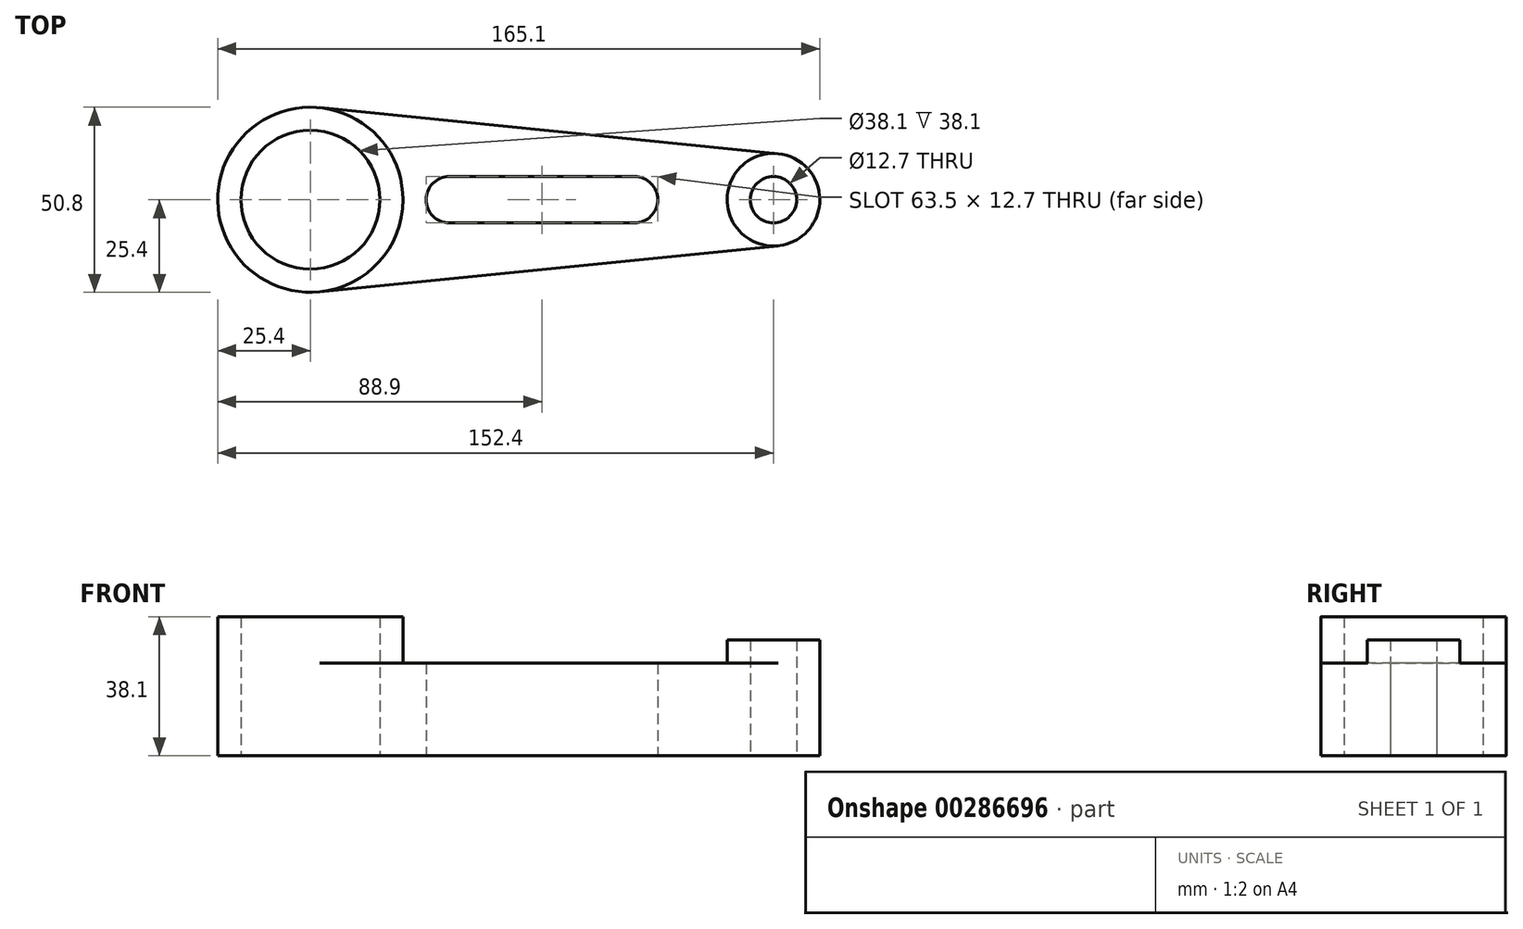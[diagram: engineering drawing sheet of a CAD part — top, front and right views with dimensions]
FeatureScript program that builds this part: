
annotation { "Feature Type Name" : "Feature", "Feature Type Description" : "" }
export const myFeature = defineFeature(function(context is Context, id is Id, definition is map)
    precondition{}
    {
        {
            var Q0;
            Q0=qCreatedBy(makeId("Top.planeOp"),FACE);
            var sketch = newSketch(context, id + "F0", { "sketchPlane" : qUnion([Q0])});
            skArc(sketch, "E0", {"start": v(0, 6.35) * mm, "mid": v(-6.35, 0) * mm, "end": v(0, -6.35) * mm});
            skLineSegment(sketch, "E1", {"start": v(0, -6.35) * mm, "end": v(50.8, -6.35) * mm});
            skLineSegment(sketch, "E2", {"start": v(0, 6.35) * mm, "end": v(50.8, 6.35) * mm});
            skArc(sketch, "E3", {"start": v(50.8, 6.35) * mm, "mid": v(57.15, 0) * mm, "end": v(50.8, -6.35) * mm});
            skCircle(sketch, "E4", {"center": v(88.9, 0) * mm, "radius": 6.35 * mm});
            skCircle(sketch, "E5", {"center": v(88.9, 0) * mm, "radius": 12.7 * mm});
            skCircle(sketch, "E6", {"center": v(-38.1, 0) * mm, "radius": 19.05 * mm});
            skCircle(sketch, "E7", {"center": v(-38.1, 0) * mm, "radius": 25.4 * mm});
            skLineSegment(sketch, "E8", {"start": v(90.17, 12.64) * mm, "end": v(-35.56, 25.27) * mm});
            skLineSegment(sketch, "E9", {"start": v(-35.56, -25.27) * mm, "end": v(90.17, -12.64) * mm});
            skSolve(sketch);
        }
        {
            var Q0;
            Q0=makeQuery(id+"F0.imprint","IMPRINT",FACE,{"disambiguationData":[TD([[makeQuery(id+"F0.imprint","IMPRINT",EDGE,{"derivedFrom":sQuery(id+"F0.wireOp",EDGE,"E6")}),-1.0]])]});
            extrude(context, id + "F1", {"entities" : qUnion([Q0]), "depth" : 38.1 * mm});
        }
        {
            var Q0;
            Q0=makeQuery(id+"F0.imprint","IMPRINT",FACE,{"disambiguationData":[TD([[makeQuery(id+"F0.imprint","IMPRINT",EDGE,{"derivedFrom":sQuery(id+"F0.wireOp",EDGE,"E0")}),-1.0]])]});
            extrude(context, id + "F2", {"entities" : qUnion([Q0]), "operationType" : NewBodyOperationType.ADD, "depth" : 25.4 * mm});
        }
        {
            var Q0;
            Q0=makeQuery(id+"F0.imprint","IMPRINT",FACE,{"disambiguationData":[TD([[makeQuery(id+"F0.imprint","IMPRINT",EDGE,{"derivedFrom":sQuery(id+"F0.wireOp",EDGE,"E4")}),-1.0]])]});
            extrude(context, id + "F3", {"entities" : qUnion([Q0]), "operationType" : NewBodyOperationType.ADD, "depth" : 31.75 * mm});
        }
    });
